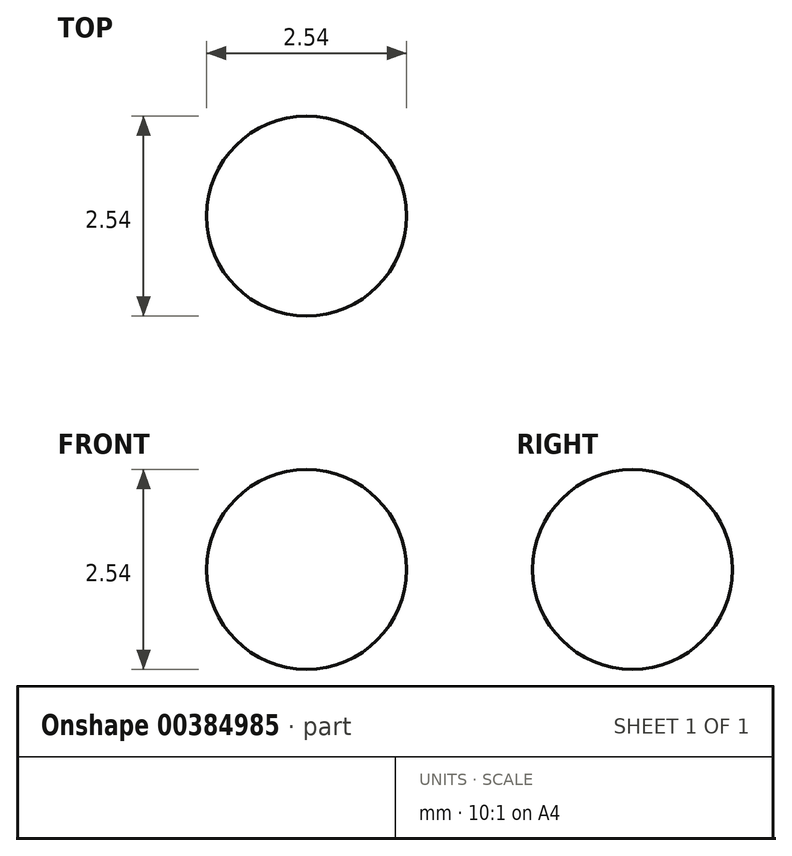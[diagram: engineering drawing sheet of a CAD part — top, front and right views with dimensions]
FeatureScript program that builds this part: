
annotation { "Feature Type Name" : "Feature", "Feature Type Description" : "" }
export const myFeature = defineFeature(function(context is Context, id is Id, definition is map)
    precondition{}
    {
        {
            var Q0;
            Q0=qCreatedBy(makeId("Top.planeOp"),FACE);
            var sketch = newSketch(context, id + "F0", { "sketchPlane" : qUnion([Q0])});
            skCircle(sketch, "E0", {"center": v(0, 0) * mm, "radius": 1.27 * mm});
            skLineSegment(sketch, "E1", {"start": v(0, 0) * mm, "end": v(0, -1.27) * mm});
            skLineSegment(sketch, "E2", {"start": v(0, -1.27) * mm, "end": v(0, 1.27) * mm});
            skSolve(sketch);
        }
        {
            var Q0;
            Q0=makeQuery(id+"F0.imprint","IMPRINT",FACE,{"disambiguationData":[TD([[makeQuery(id+"F0.imprint","IMPRINT",EDGE,{"derivedFrom":sQuery(id+"F0.wireOp",EDGE,"E0")}),1.0]])]});
            var sketch = newSketch(context, id + "F1", { "sketchPlane" : qUnion([Q0])});
            skLineSegment(sketch, "E3", {"start": v(0, 0) * mm, "end": v(0, -6.91) * mm});
            skLineSegment(sketch, "E4", {"start": v(0, -6.91) * mm, "end": v(0, 6.97) * mm});
            skSolve(sketch);
        }
        {
            var Q0;
            {var subQ0=sQuery(id+"F0.wireOp",EDGE,"E2");var subQ4=makeQuery(id+"F0.imprint","IMPRINT",VERTEX,{"derivedFrom":subQ0});Q0=makeQuery(id+"F0.imprint","IMPRINT",FACE,{"disambiguationData":[TD([[makeQuery(id+"F0.imprint","IMPRINT",EDGE,{"disambiguationData":[TD([[subQ4,1.0]])],"derivedFrom":subQ0}),-1.0]])]});}
            var Q1;
            Q1=sQuery(id+"F1.wireOp",EDGE,"E4");
            revolve(context, id + "F2", {"entities" : qUnion([Q0]), "axis" : qUnion([Q1]), "revolveType" : RevolveType.FULL});
        }
    });
